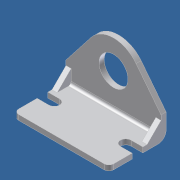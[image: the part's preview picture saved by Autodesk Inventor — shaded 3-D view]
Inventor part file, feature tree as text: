
AUTODESK INVENTOR PART (.ipt)
format: ipt  version: unknown  size: 257,536 bytes
history: native  units: in
note: dims shown in document units (in); Inventor stores cm internally (conversion verified against a paired STEP export)
features: other x126, extrude x9, sketch x9
ambient origin geometry x8: Origin, YZ Plane, XZ Plane, XY Plane, X Axis, Y Axis, Z Axis, Center Point
feature tree (144):
  extrude  "Extrusion1"  Depth=0.2018in TaperAngle=0.0deg
  extrude  "Extrusion2"  Depth=0.2018in TaperAngle=0.0deg
  extrude  "Extrusion3"  Depth=0.2018in TaperAngle=0.0deg
  extrude  "Extrusion4"  Depth=0.1345in TaperAngle=0.0deg
  extrude  "Extrusion5"  [1 undecoded]
  extrude  "Extrusion6"  [1 undecoded]
  extrude  "Extrusion7"  [1 undecoded]
  extrude  "Extrusion8"  [1 undecoded]
  extrude  "Extrusion9"  [1 undecoded]
  other  "d1_XY"
  other  "d1_YZ"
  other  "d1_ZX"
  other  "d1_X"
  other  "d1_Y"
  other  "d1_Z"
  other  "d1_Center"
  other  "d2_XY"
  other  "d2_YZ"
  other  "d2_ZX"
  other  "d2_X"
  other  "d2_Y"
  other  "d2_Z"
  other  "d2_Center"
  other  "h1_XY"
  other  "h1_YZ"
  other  "h1_ZX"
  other  "h1_X"
  other  "h1_Y"
  other  "h1_Z"
  other  "h1_Center"
  other  "h2_XY"
  other  "h2_YZ"
  other  "h2_ZX"
  other  "h2_X"
  other  "h2_Y"
  other  "h2_Z"
  other  "h2_Center"
  other  "h3_XY"
  other  "h3_YZ"
  other  "h3_ZX"
  other  "h3_X"
  other  "h3_Y"
  other  "h3_Z"
  other  "h3_Center"
  other  "h4_XY"
  other  "h4_YZ"
  other  "h4_ZX"
  other  "h4_X"
  other  "h4_Y"
  other  "h4_Z"
  other  "h4_Center"
  other  "h5_XY"
  other  "h5_YZ"
  other  "h5_ZX"
  other  "h5_X"
  other  "h5_Y"
  other  "h5_Z"
  other  "h5_Center"
  other  "h6_XY"
  other  "h6_YZ"
  other  "h6_ZX"
  other  "h6_X"
  other  "h6_Y"
  other  "h6_Z"
  other  "h6_Center"
  other  "l1_XY"
  other  "l1_YZ"
  other  "l1_ZX"
  other  "l1_X"
  other  "l1_Y"
  other  "l1_Z"
  other  "l1_Center"
  other  "l2_XY"
  other  "l2_YZ"
  other  "l2_ZX"
  other  "l2_X"
  other  "l2_Y"
  other  "l2_Z"
  other  "l2_Center"
  other  "l3_XY"
  other  "l3_YZ"
  other  "l3_ZX"
  other  "l3_X"
  other  "l3_Y"
  other  "l3_Z"
  other  "l3_Center"
  other  "l4_XY"
  other  "l4_YZ"
  other  "l4_ZX"
  other  "l4_X"
  other  "l4_Y"
  other  "l4_Z"
  other  "l4_Center"
  other  "l5_XY"
  other  "l5_YZ"
  other  "l5_ZX"
  other  "l5_X"
  other  "l5_Y"
  other  "l5_Z"
  other  "l5_Center"
  other  "l6_XY"
  other  "l6_YZ"
  other  "l6_ZX"
  other  "l6_X"
  other  "l6_Y"
  other  "l6_Z"
  other  "l6_Center"
  other  "l7_XY"
  other  "l7_YZ"
  other  "l7_ZX"
  other  "l7_X"
  other  "l7_Y"
  other  "l7_Z"
  other  "l7_Center"
  other  "l8_XY"
  other  "l8_YZ"
  other  "l8_ZX"
  other  "l8_X"
  other  "l8_Y"
  other  "l8_Z"
  other  "l8_Center"
  other  "mounting_bracket_XY"
  other  "mounting_bracket_YZ"
  other  "mounting_bracket_ZX"
  other  "mounting_bracket_X"
  other  "mounting_bracket_Y"
  other  "mounting_bracket_Z"
  other  "mounting_bracket_Center"
  other  "mounting_bracket_1_XY"
  other  "mounting_bracket_1_YZ"
  other  "mounting_bracket_1_ZX"
  other  "mounting_bracket_1_X"
  other  "mounting_bracket_1_Y"
  other  "mounting_bracket_1_Z"
  other  "mounting_bracket_1_Center"
  sketch  "Sketch_1"  dims[d0=2.49in d1=0.0in d2=0.2018in d3=0.0in]
  sketch  "Sketch_2"  dims[d4=0.2018in d5=0.0in d6=0.2018in d7=0.0in]
  sketch  "Sketch_3"  dims[d8=0.2018in d9=0.0in d10=0.2018in d11=0.0in]
  sketch  "Sketch_6"  dims[d12=0.2018in d13=0.0in d14=0.1345in d15=0.0in]
  sketch  "Sketch_7"  dims[d16=0.1345in d17=0.0in]
  sketch  "Sketch_8"
  sketch  "Sketch_9"
  sketch  "Sketch_12"
  sketch  "Sketch_13"
note: 5 required parameter values undecoded (feature->parameter linkage not recoverable at this tier; creation-order binding heuristic only, values carry confidence <= 0.55)
